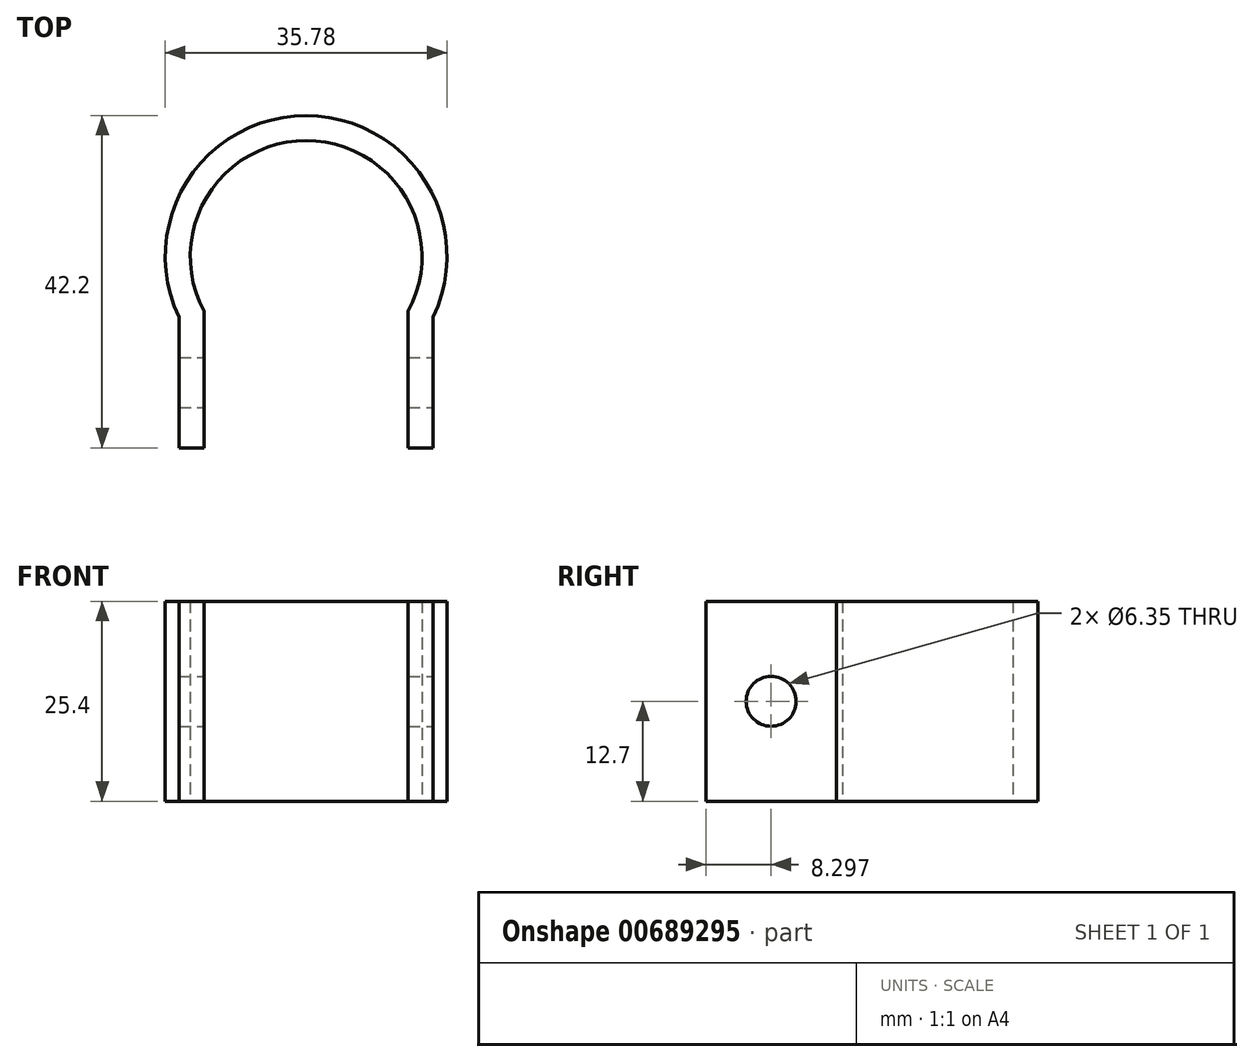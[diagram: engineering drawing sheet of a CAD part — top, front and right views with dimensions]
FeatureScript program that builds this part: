
annotation { "Feature Type Name" : "Feature", "Feature Type Description" : "" }
export const myFeature = defineFeature(function(context is Context, id is Id, definition is map)
    precondition{}
    {
        {
            var Q0;
            Q0=qCreatedBy(makeId("Top.planeOp"),FACE);
            var sketch = newSketch(context, id + "F0", { "sketchPlane" : qUnion([Q0])});
            skArc(sketch, "E0", {"start": v(12.97, -6.96) * mm, "mid": v(0, 14.72) * mm, "end": v(-12.97, -6.96) * mm});
            skLineSegment(sketch, "E1", {"start": v(-12.97, -6.96) * mm, "end": v(-12.97, -24.3) * mm});
            skLineSegment(sketch, "E2", {"start": v(12.97, -6.96) * mm, "end": v(12.97, -24.3) * mm});
            skLineSegment(sketch, "E3.0", {"start": v(-16.14, -7.72) * mm, "end": v(-16.14, -24.3) * mm});
            skArc(sketch, "E3.1", {"start": v(16.14, -7.72) * mm, "mid": v(0, 17.9) * mm, "end": v(-16.14, -7.72) * mm});
            skLineSegment(sketch, "E3.2", {"start": v(16.14, -7.72) * mm, "end": v(16.14, -24.3) * mm});
            skLineSegment(sketch, "E4", {"start": v(-16.14, -24.3) * mm, "end": v(-12.97, -24.3) * mm});
            skLineSegment(sketch, "E5", {"start": v(12.97, -24.3) * mm, "end": v(16.14, -24.3) * mm});
            skSolve(sketch);
        }
        {
            var Q0;
            Q0=qSketchRegion(id+"F0",true);
            extrude(context, id + "F1", {"entities" : qUnion([Q0]), "depth" : 25.4 * mm});
        }
        {
            var Q0;
            Q0=makeQuery(id+"F1.opExtrude","SWEPT_FACE",FACE,{"disambiguationData":[OSD([sQuery(id+"F0.wireOp",EDGE,"E3.2")])]});
            var sketch = newSketch(context, id + "F2", { "sketchPlane" : qUnion([Q0])});
            skCircle(sketch, "E6", {"center": v(-16.01, 12.7) * mm, "radius": 3.18 * mm});
            skLineSegment(sketch, "E7", {"start": v(-7.72, 25.4) * mm, "end": v(-24.3, 0) * mm});
            skSolve(sketch);
        }
        {
            var Q0;
            Q0=makeQuery(id+"F2.imprint","IMPRINT",FACE,{"disambiguationData":[TD([[makeQuery(id+"F2.imprint","IMPRINT",EDGE,{"derivedFrom":sQuery(id+"F2.wireOp",EDGE,"E6")}),1.0]])]});
            extrude(context, id + "F3", {"entities" : qUnion([Q0]), "operationType" : NewBodyOperationType.REMOVE, "oppositeDirection" : true, "depth" : 63.5 * mm});
        }
    });
